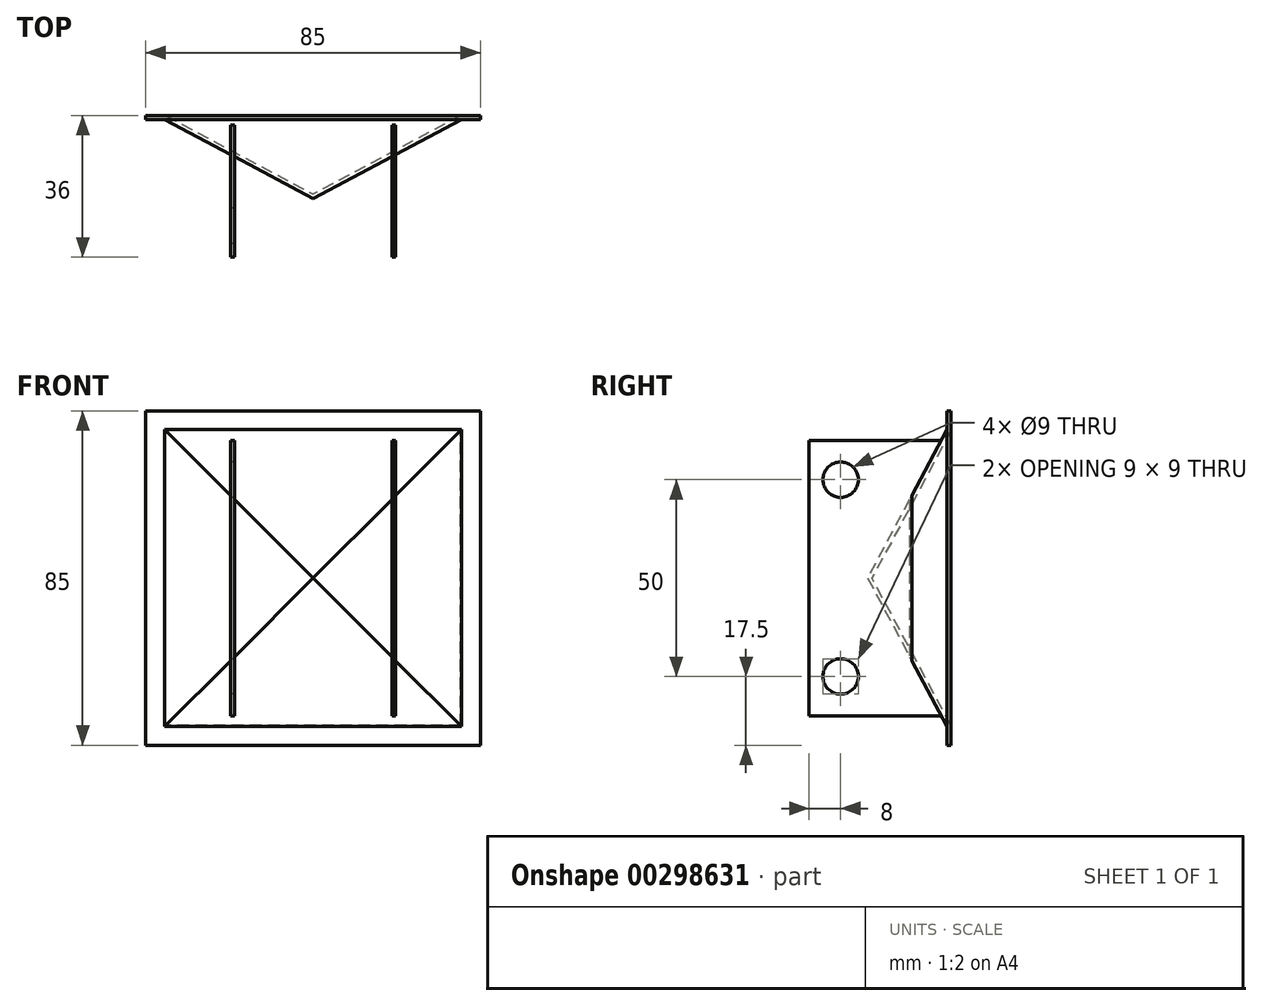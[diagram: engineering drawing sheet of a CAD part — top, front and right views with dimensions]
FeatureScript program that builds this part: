
annotation { "Feature Type Name" : "Feature", "Feature Type Description" : "" }
export const myFeature = defineFeature(function(context is Context, id is Id, definition is map)
    precondition{}
    {
        {
            var Q0;
            Q0=qCreatedBy(makeId("Front.planeOp"),FACE);
            var sketch = newSketch(context, id + "F0", { "sketchPlane" : qUnion([Q0])});
            skLineSegment(sketch, "E0.bottom", {"start": v(42.5, -42.5) * mm, "end": v(-42.5, -42.5) * mm});
            skLineSegment(sketch, "E0.top", {"start": v(42.5, 42.5) * mm, "end": v(-42.5, 42.5) * mm});
            skLineSegment(sketch, "E0.left", {"start": v(42.5, -42.5) * mm, "end": v(42.5, 42.5) * mm});
            skLineSegment(sketch, "E0.right", {"start": v(-42.5, -42.5) * mm, "end": v(-42.5, 42.5) * mm});
            skPoint(sketch, "E0.middle", {"position": v(0, 0) * mm});
            skLineSegment(sketch, "E1.bottom", {"start": v(37.5, -37.5) * mm, "end": v(-37.5, -37.5) * mm});
            skLineSegment(sketch, "E1.top", {"start": v(37.5, 37.5) * mm, "end": v(-37.5, 37.5) * mm});
            skLineSegment(sketch, "E1.left", {"start": v(37.5, -37.5) * mm, "end": v(37.5, 37.5) * mm});
            skLineSegment(sketch, "E1.right", {"start": v(-37.5, -37.5) * mm, "end": v(-37.5, 37.5) * mm});
            skSolve(sketch);
        }
        {
            var Q0;
            Q0=qCreatedBy(makeId("Front.planeOp"),FACE);
            cPlane(context, id + "F1", {"entities" : qUnion([Q0]), "cplaneType" : CPlaneType.OFFSET, "offset" : 20 * mm, "width" : 150 * mm, "height" : 150 * mm});
        }
        {
            var Q0;
            Q0=qCreatedBy(id+"F1.planeOp",FACE);
            var sketch = newSketch(context, id + "F2", { "sketchPlane" : qUnion([Q0])});
            skPoint(sketch, "E2", {"position": v(0, 0) * mm});
            skSolve(sketch);
        }
        {
            var Q0;
            Q0=makeQuery(id+"F0.imprint","IMPRINT",FACE,{"disambiguationData":[TD([[makeQuery(id+"F0.imprint","IMPRINT",EDGE,{"derivedFrom":sQuery(id+"F0.wireOp",EDGE,"E1.bottom")}),-1.0]])]});
            var Q1;
            Q1=sQuery(id+"F2.wireOp",VERTEX,"E2");
            loft(context, id + "F3", {"sheetProfilesArray" : [{ "sheetProfileEntities" : qUnion([Q0]) }, { "sheetProfileEntities" : qUnion([Q1]) }]});
        }
        {
            var Q0;
            Q0=makeQuery(id+"F3.opLoft","CAP_FACE",FACE,{"disambiguationData":[OSD([makeQuery(id+"F0.imprint","IMPRINT",FACE,{"disambiguationData":[TD([[makeQuery(id+"F0.imprint","IMPRINT",EDGE,{"derivedFrom":sQuery(id+"F0.wireOp",EDGE,"E1.bottom")}),-1.0]])]})])],"isStart":true});
            shell(context, id + "F4", {"entities" : qUnion([Q0]), "thickness" : 1 * mm, "oppositeDirection" : true});
        }
        {
            var Q0;
            Q0=makeQuery(id+"F0.imprint","IMPRINT",FACE,{"disambiguationData":[TD([[makeQuery(id+"F0.imprint","IMPRINT",EDGE,{"derivedFrom":sQuery(id+"F0.wireOp",EDGE,"E0.bottom")}),-1.0]])]});
            extrude(context, id + "F5", {"entities" : qUnion([Q0]), "operationType" : NewBodyOperationType.ADD, "depth" : 1 * mm});
        }
        {
            var Q0;
            Q0=qCreatedBy(id+"F1.planeOp",FACE);
            cPlane(context, id + "F6", {"entities" : qUnion([Q0]), "cplaneType" : CPlaneType.OFFSET, "offset" : 16 * mm, "width" : 150 * mm, "height" : 150 * mm});
        }
        {
            var Q0;
            Q0=qCreatedBy(id+"F6.planeOp",FACE);
            var sketch = newSketch(context, id + "F7", { "sketchPlane" : qUnion([Q0])});
            skLineSegment(sketch, "E3", {"start": v(-21, 34.98) * mm, "end": v(-21, -35.02) * mm});
            skLineSegment(sketch, "E4", {"start": v(-21, -35.02) * mm, "end": v(-20, -35.02) * mm});
            skLineSegment(sketch, "E5", {"start": v(-20, -35.02) * mm, "end": v(-20, 35) * mm});
            skLineSegment(sketch, "E6", {"start": v(-20, 35) * mm, "end": v(-21, 34.98) * mm});
            skLineSegment(sketch, "E7", {"start": v(0, 7.44) * mm, "end": v(0, -7.9) * mm, "construction": true});
            skLineSegment(sketch, "E8.MirrorCS", {"start": v(20, -35.02) * mm, "end": v(20, 35) * mm});
            skLineSegment(sketch, "E9.MirrorCS", {"start": v(21, 34.98) * mm, "end": v(21, -35.02) * mm});
            skLineSegment(sketch, "E10.MirrorCS", {"start": v(20, 35) * mm, "end": v(21, 34.98) * mm});
            skLineSegment(sketch, "E11.MirrorCS", {"start": v(21, -35.02) * mm, "end": v(20, -35.02) * mm});
            skSolve(sketch);
        }
        {
            var Q0;
            Q0=makeQuery(id+"F7.imprint","IMPRINT",FACE,{"disambiguationData":[TD([[makeQuery(id+"F7.imprint","IMPRINT",EDGE,{"derivedFrom":sQuery(id+"F7.wireOp",EDGE,"E3")}),1.0]])]});
            var Q1;
            Q1=makeQuery(id+"F7.imprint","IMPRINT",FACE,{"disambiguationData":[TD([[makeQuery(id+"F7.imprint","IMPRINT",EDGE,{"derivedFrom":sQuery(id+"F7.wireOp",EDGE,"E8.MirrorCS")}),-1.0]])]});
            extrude(context, id + "F8", {"entities" : qUnion([Q0, Q1]), "operationType" : NewBodyOperationType.ADD, "endBound" : BoundingType.UP_TO_NEXT, "oppositeDirection" : true, "depth" : 25 * mm});
        }
        {
            var Q0;
            Q0=makeQuery(id+"F8.opExtrude","SWEPT_FACE",FACE,{"disambiguationData":[OSD([sQuery(id+"F7.wireOp",EDGE,"E3")])]});
            var sketch = newSketch(context, id + "F9", { "sketchPlane" : qUnion([Q0])});
            skLineSegment(sketch, "E12", {"start": v(28, 31.83) * mm, "end": v(28, -34.78) * mm, "construction": true});
            skCircle(sketch, "E13", {"center": v(28, 25) * mm, "radius": 4.5 * mm});
            skCircle(sketch, "E14", {"center": v(28, -25) * mm, "radius": 4.5 * mm});
            skSolve(sketch);
        }
        {
            var Q0;
            Q0=makeQuery(id+"F9.imprint","IMPRINT",FACE,{"disambiguationData":[TD([[makeQuery(id+"F9.imprint","IMPRINT",EDGE,{"derivedFrom":sQuery(id+"F9.wireOp",EDGE,"E13")}),1.0]])]});
            var Q1;
            Q1=makeQuery(id+"F9.imprint","IMPRINT",FACE,{"disambiguationData":[TD([[makeQuery(id+"F9.imprint","IMPRINT",EDGE,{"derivedFrom":sQuery(id+"F9.wireOp",EDGE,"E14")}),1.0]])]});
            extrude(context, id + "F10", {"entities" : qUnion([Q0, Q1]), "operationType" : NewBodyOperationType.REMOVE, "endBound" : BoundingType.THROUGH_ALL, "oppositeDirection" : true, "depth" : 25 * mm});
        }
    });
